# Revit family: PD4-C-FP types Avec hôte
name_source: partatom
category: Dispositifs d'éclairage
units: mm (PartAtom-declared; Revit-internal decimal feet)

## family parameters
Conserver l'orientation des annotations = Oui
Cote de connecteur circulaire = Utiliser le diamètre
Couper avec des vides une fois chargée = Non
Hôte = Face
Partagée = Non
Point de calcul de pièce = Non
Type d'élément = Normal

## types (15) — shared parameters
Classe = II
Code d'assemblage = D5010200
Fabricant = B.E.G.
Hauteur de montage max = 280 cm
Image du type = COULOIR.jpg
Marque = LUXOMAT
Mode de pose = Faux plafond
Température ambiante = -25°C à +50°C
URL = http://www.luxomat.com
zero-valued in all types: Elévation par défaut

## per-type parameters (varying)
| type | Alimentation | Charge Cos ɸ =0.5 | Charge Cos ɸ =1 | Charge LED | Commentaires du type | Consommation | IP | Modèle | Relais | Référence | Type de Sortie |
| 01- PD4-C-FP Générique | 110-240 V AC |  |  |  | DET.PRES.SPECIAL COULOIR.180/360°/2x10M FAUX PLAFOND |  | 20 | PD4-C-FP |  |  |  |
| 02- PD4N-1C-C-FP réf 92274 | 110-240 V AC | 1150 VA | 2300 W | 300 W | DET.MOUV.SPECIAL COULOIR.1 CONTACT.180/360°/2x10M FAUX PLAFOND | 0,25 W | 23 | PD4N-1C-C-FP | 10 A | 92274 | TOR |
| 03- PD4-M-1C-C-FP réf 92586 | 110-240 V AC | 1150 VA | 2300 W | 300 W | DET.PRES.SPECIAL COULOIR.MAITRE.1 CONTACT.180/360°/2x10M FAUX PLAFOND | 0,45 W | 20 | PD4-M-1C-C-FP | 10 A | 92586 | TOR |
| 04- PD4-M-1C-C-SP-FP réf 92480 | 110-240 V AC | 1150 VA | 2300 W | 300 W | DET.PRES.SPECIAL COULOIR.MAITRE.1 CONTACT.SECURITE POSITIVE.180/360°/2x10M FAUX PLAFOND | 0,45 W | 20 | PD4-M-1C-C-SP-FP | 10 A | 92480 | TOR / Sécurité Positive |
| 05- PD4-M-2C-C-FP réf 92143 | 110-240 V AC | 1150 VA | 2300 W | 300 W | DET.PRES.SPECIAL COULOIR.MAITRE.2 CONTACTS.180/360°/2x10M FAUX PLAFOND | 0,47 W | 20 | PD4-M-2C-C-FP | 10 A / 3 A | 92143 | TOR + CVC |
| 08- PD4-M-DIM-C-FP réf 92217 | 110-240 V AC | 1150 VA | 2300 W | 300 W | DET.PRES.SPECIAL COULOIR.MAITRE.DIM(1-10V).180/360°/2x10M FAUX PLAFOND | 0,50 W | 20 | PD4-M-DIM-C-FP | 10 A | 92217 | DIM (50 ballasts maxi) |
| 06- PD4N-M-DACO-C-FP réf 93460 | 110-240 V AC | 0 | 0 | 0 | DET.PRES.SPECIAL COULOIR.MAITRE.DALI 2.180/360°/2x10M FAUX PLAFOND + Lentille Couloir réf 93073 | 2 W | 20 | PD4N-M-DACO-C-FP | 0 | 93460+93073 | DALI 2  (40 drivers maxi) |
| 13- PD4N-KNX-C-DX-FP réf 93388 | 24 V DC par Bus KNX | 0 | 0 | 0 | DET.PRES.SPECIAL COULOIR.KNX.VERSION DELUXE.180/360°/2x10M FAUX PLAFOND | 12 mA | 20 | PD4N-KNX-C-DX-FP | 0 | 93388 | KNX - 1 sortie Eclairage TOR ou GRADATION / 3 sorties Présence / Capteur de température et bruit |
| 09- PD4-S-C-FP réf 92444 | 110-240 V AC | 0 | 0 | 0 | DET.PRES.SPECIAL COULOIR.ESCLAVE.180/360°/2x10M FAUX PLAFOND | 0,25 W | 20 | PD4-S-C-FP | 0 | 92444 | Esclave |
| 12- PD4N-BMS-DALI-2-C-FP réf 93546 | 10-22 V DC par Bus DALI | 0 | 0 | 0 | MULTI.CAPTEUR.PRES.SPECIAL COULOIR.BMS.DALI 2.180/360°/2x10M FAUX PLAFOND + Lentille Couloir réf 93073 | 7 mA | 20 | PD4N-BMS-DALI-2-C-FP | 0 | 93546+93073 | DALI 2 adressable - BMS |
| 11- PD4N-DALISYS-C-FP réf 93340 | 10-22 V DC par Bus DALI | 0 | 0 | 0 | MULTI.CAPTEUR.PRES.SPECIAL COULOIR.DALISYS.180/360°/2x10M FAUX PLAFOND + Lentille Couloir réf 93073 | 7 mA | 20 | PD4N-DALISYS-C-FP | 0 | 93340+93073 | DALI adressable |
| 10- PD4N-DALILINK-C-FP réf 93377 | 16 V DC par Bus DALI | 0 | 0 | 0 | MULTI.CAPTEUR.PRES.SPECIAL COULOIR.DALILINK.180/360°/2x10M FAUX PLAFOND + Lentille Couloir réf 93073 | 7 mA | 20 | PD4N-DALILINK-C-FP | 0 | 93377+93073 | DALILINK |
| 14- PD4N-KNXs-C-ST-FP réf 93514 | 24 V DC par Bus KNX | 0 | 0 | 0 | DET.PRES.SPECIAL COULOIR.KNX Sécure.VERSION STANDARD.180/360°/2x10M FAUX PLAFOND + Lentille Couloir réf 93073 | 12 mA | 20 | PD4N-KNXs-C-ST-FP | 0 | 93514+93073 | KNX Sécure - 1 sortie Eclairage TOR ou GRADATION / 3 sorties Présence / HCL |
| 15- PD4N-KNXs-C-DX-FP réf 93516 | 24 V DC par Bus KNX | 0 | 0 | 0 | DET.PRES.SPECIAL COULOIR.KNX Sécure.VERSION DELUXE.180/360°/2x10M FAUX PLAFOND + Lentille Couloir réf 93073 | 12 mA | 20 | PD4N-KNXs-C-DX-FP | 0 | 93516+93073 | KNX Sécure - 1 sortie Eclairage TOR ou GRADATION / 3 sorties Présence / Capteur de température et bruit / HCL |
| 07- PD4N-M-DACO-1C-C-FP réf 93463 | 110-240 V AC | 1150 VA | 2300 W | 300 W | DET.PRES.SPECIAL COULOIR.MAITRE.DALI 2 + CONTACT NO.180/360°/2x10M FAUX PLAFOND + Lentille Couloir réf 93073 | 2 W | 20 | PD4N-M-DACO-1C-C-FP | 10 A | 93463+93073 | DALI 2 (40 drivers maxi) + Contact NO |
